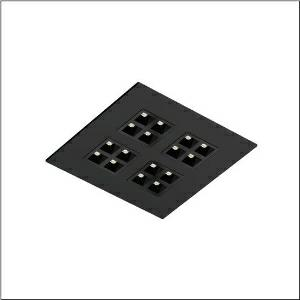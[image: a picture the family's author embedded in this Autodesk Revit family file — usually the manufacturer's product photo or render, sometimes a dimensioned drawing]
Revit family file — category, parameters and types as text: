
# Revit family: silica_r__31_square_51my6lms34ba_bf29
name_source: partatom
category: Lighting Fixtures
units: mm (PartAtom-declared; Revit-internal decimal feet)

## family parameters
Cut with Voids When Loaded = No
Host = Face
Light Source = No
Part Type = Normal
Room Calculation Point = No
Round Connector Dimension = Use Diameter
Shared = No

## types (1)
- --- (1 x LED, 6250 lm, 39 W, 3000K)
    Apparent Load = 39 VA
    CIE Flux Codes = 82 100 100 100 100
    Color Rendering = 80
    Color Temperature = 3000K
    Default Elevation = 1800 mm
    Description = Silica® 31 Square, office luminaire, primary light control with lens, of PMMA, primary anti-glare with reflector, of PC, black, light emission: direct distribution, primary light characteristic: symmetric, installation type: lay-in mounting, LED, rated luminous flux: 4.600lm, luminous efficacy: 166lm/W, light colour: 830, colour temperature: 3000K, control gear: ON/OFF Multilumen, with terminal, 3-pole, mains connection: 220..240V, AC, 50/60Hz, rated input power: 27.7W, luminaire housing, of sheet steel, coated, jet black (RAL 9005), module: M600, length: 595mm, width: 595mm, height: 43mm, protection rating (complete): IP20, insulation class (complete): insulation class II (safety insulation), certification: CE, impact resistance: IK03, permissible operating ambient temperature: -20..+35°C, standard: EN 50419, packaging unit: 1 piece
    Height = 0 mm  [stored 0 ft]
    Lamp = 1 x LED
    Lamp Light Flux = 6250 lm
    Lamp Power = 39 W
    Lamp count = 1
    Length = 595 mm
    Luminous efficacy = 160 lm/W
    Manufacturer = Siteco
    ModVariant = No
    Model = 51MY6LMS34BA
    Mounting Place = Ceiling
    Mounting Type = Recessed
    Number of Poles = 1
    OnlyDefault = Yes
    Power Factor = 1
    Product Name = Silica® 31 Square
    Product group = office luminaire | ceiling recessed
    ProductGroupID = 400
    Protection Class = Protection class II
    Protection Degree = IP 20
    RLX_Detail_Level = 1
    RLX_Emergency_Light_Flux = 0 lm
    RLX_Emergency_Type = 0
    RLX_Emergency_Type_DB = No
    RlxData = <blob elided: 36221 chars, md5=7f8ebcb8>
    Socket = socket
    Standby Power = 0 W
    System Light Flux = 6250 lm
    System Power = 39 W
    Type Comments = factory setting: luminous flux: 100 % | (ON | ON | ON | ON) | 1100 mA
    Type Image = l_1313660.jpg
    URL = http://relux.com
    VarID = @adj_056601
    Voltage = 0 V
    Weight = 0.00 kg
    Width = 595 mm

note: [stored X ft] marks values corroborated as IEEE doubles in the binary element streams (Revit-internal decimal feet)

## geometry (parser evidence)
native form markers: Blend x4, Sweep x11
no freeform markers — native parametric forms only
